FCSTD DOCUMENT  (FreeCAD 1.0RUnknown)
Label: wardrobe_corpus03_jan_assy4
License: All rights reserved
LicenseURL: https://en.wikipedia.org/wiki/All_rights_reserved
objects: App::Link×7, App::DocumentObjectGroup×3, Part::FeaturePython×2, PartDesign::CoordinateSystem×1, App::FeaturePython×1, App::Part×1, Assembly::BomObject×1
note: 3 computed .brp shape members not serialized (recipe doc carries the construction recipe); baked Part::Feature solids carry a one-line shape summary decoded from their .brp
EXTERNAL_REF file=parts/wardrobe_base_corpus03_jan.FCStd obj=LCS_Origin
EXTERNAL_REF file=parts/wardrobe_base_corpus03_jan.FCStd obj=wardrobe_base_corpus03_jan
EXTERNAL_REF file=parts/wardrobe_base_corpus03_jan.FCStd obj=LCS_1
EXTERNAL_REF file=parts/wardrobe_left_corpus03_jan.FCStd obj=LCS_1
EXTERNAL_REF file=parts/wardrobe_left_corpus03_jan.FCStd obj=wardrobe_left_corpus03_jan
EXTERNAL_REF file=parts/wardrobe_base_corpus03_jan.FCStd obj=LCS_right
EXTERNAL_REF file=parts/wardrobe_right_corpus03_jan.FCStd obj=LCS_1
EXTERNAL_REF file=parts/wardrobe_right_corpus03_jan.FCStd obj=wardrobe_right_corpus03_jan
EXTERNAL_REF file=parts/wardrobe_left_corpus03_jan.FCStd obj=LCS_2
EXTERNAL_REF file=parts/wardrobe_top_corpus03_jan.FCStd obj=LCS_1
EXTERNAL_REF file=parts/wardrobe_top_corpus03_jan.FCStd obj=wardrobe_top_corpus03_jan
EXTERNAL_REF file=../purchased parts/hettich-level-adjustment.FCStd obj=LCS_Origin
EXTERNAL_REF file=parts/wardrobe_base_corpus03_jan.FCStd obj=LCS_2
EXTERNAL_REF file=../purchased parts/hettich-level-adjustment.FCStd obj=hettich_level_adjustment
EXTERNAL_REF file=../mastersketch.FCStd obj=Sketch001
EXTERNAL_REF file=parts/wardrobe_backplate_corpus03_jan.FCStd obj=LCS_1
EXTERNAL_REF file=parts/wardrobe_base_corpus03_jan.FCStd obj=LCS_back
EXTERNAL_REF file=parts/wardrobe_backplate_corpus03_jan.FCStd obj=wardrobe_backplate_corpus03_jan
EXTERNAL_REF file=parts/wardrobe_base_corpus03_jan.FCStd obj=LCS_door
EXTERNAL_REF file=parts/wardrobe_door_03_jan.FCStd obj=LCS_Origin
EXTERNAL_REF file=parts/wardrobe_door_03_jan.FCStd obj=wardrobe_door_03_jan

FEATURE [App::DocumentObjectGroup] Parts
FEATURE [PartDesign::CoordinateSystem] LCS_Origin
  AttacherType = Attacher::AttachEngine3D
  AttachmentSupport = -> [X_Axis]
  MapMode = 2
FEATURE [App::DocumentObjectGroup] Constraints
FEATURE [App::FeaturePython] Variables  # WARN: FeaturePython — macro-defined, semantics opaque (R4)
  Type = App::PropertyContainer
FEATURE [App::DocumentObjectGroup] Configurations
FEATURE [App::Link] wardrobe_base_corpus03_jan001
  AttachedBy = #LCS_Origin
  AttachedTo = Parent Assembly#LCS_Origin
  LinkedObject = -> <external parts/wardrobe_base_corpus03_jan.FCStd>#wardrobe_base_corpus03_jan
  SolverId = Asm4EE
  expr: Placement = LCS_Origin.Placement * AttachmentOffset * wardrobe_base_corpus03_jan#LCS_Origin.Placement ^ -1
FEATURE [App::Link] wardrobe_left_corpus03_jan001
  AttachedBy = #LCS_1
  AttachedTo = wardrobe_base_corpus03_jan001#LCS_1
  AttachmentOffset = pos=(0,0,0) rot=(0,1,0;3.14159rad)
  LinkPlacement = pos=(-260,300,19) rot=(0,0,1;4.71239rad)
  LinkedObject = -> <external parts/wardrobe_left_corpus03_jan.FCStd>#wardrobe_left_corpus03_jan
  Placement = pos=(-260,300,19) rot=(0,0,1;4.71239rad)
  SolverId = Asm4EE
  expr: Placement = wardrobe_base_corpus03_jan001.Placement * wardrobe_base_corpus03_jan#LCS_1.Placement * AttachmentOffset * wardrobe_left_corpus03_jan#LCS_1.Placement ^ -1
FEATURE [App::Link] wardrobe_right_corpus03_jan001
  AttachedBy = #LCS_1
  AttachedTo = wardrobe_base_corpus03_jan001#LCS_right
  LinkPlacement = pos=(260,300,19) rot=(0,0,1;0rad)
  LinkedObject = -> <external parts/wardrobe_right_corpus03_jan.FCStd>#wardrobe_right_corpus03_jan
  Placement = pos=(260,300,19) rot=(0,0,1;0rad)
  SolverId = Asm4EE
  expr: Placement = wardrobe_base_corpus03_jan001.Placement * wardrobe_base_corpus03_jan#LCS_right.Placement * AttachmentOffset * wardrobe_right_corpus03_jan#LCS_1.Placement ^ -1
FEATURE [App::Link] wardrobe_top_corpus03_jan001
  AttachedBy = #LCS_1
  AttachedTo = wardrobe_left_corpus03_jan001#LCS_2
  AttachmentOffset = pos=(0,0,0) rot=(0,1,0;3.14159rad)
  LinkPlacement = pos=(5.68e-14,300,465.913) rot=(0,1,0;5.41956rad)
  LinkedObject = -> <external parts/wardrobe_top_corpus03_jan.FCStd>#wardrobe_top_corpus03_jan
  Placement = pos=(5.68e-14,300,465.913) rot=(0,1,0;5.41956rad)
  SolverId = Asm4EE
  expr: Placement = wardrobe_left_corpus03_jan001.Placement * wardrobe_left_corpus03_jan#LCS_2.Placement * AttachmentOffset * wardrobe_top_corpus03_jan#LCS_1.Placement ^ -1
FEATURE [App::Link] hettich_level_adjustment
  AttachedBy = #LCS_Origin
  AttachedTo = wardrobe_base_corpus03_jan001#LCS_2
  AttachmentOffset = pos=(0,0,0) rot=(0.707107,0.707107,0;3.14159rad)
  LinkPlacement = pos=(-220,-230,0) rot=(0.707107,0.707107,0;3.14159rad)
  LinkedObject = -> <external ../purchased parts/hettich-level-adjustment.FCStd>#hettich_level_adjustment
  Placement = pos=(-220,-230,0) rot=(0.707107,0.707107,0;3.14159rad)
  SolverId = Asm4EE
  expr: Placement = wardrobe_base_corpus03_jan001.Placement * wardrobe_base_corpus03_jan#LCS_2.Placement * AttachmentOffset * hettich_level_adjustment#LCS_Origin.Placement ^ -1
FEATURE [Part::FeaturePython] Linear_hettich_level_adjustment  # Draft array (typed FeaturePython)
  ArrayType = Linear Array
  Axis = -> X_Axis
  AxisPlacement = pos=(0,0,0) rot=(0.57735,0.57735,0.57735;2.0944rad)
  Count = 2
  Index = 1
  LinearStep = 440
  PlacementList = 2 placements: [(-220,-230,6.31089e-30),(220,-230,4.88498e-14)]
  Placer = pos=(0,0,440) rot=(0,0,1;0rad)
  ScaleList = (2) [(1,1,1),(1,1,1)]
  Scaler = 1
  ShowElement = false
  SourceObject = -> hettich_level_adjustment
  expr: .Placer.Base.z = LinearStep * Index
  expr: LinearStep = mastersketch#<<corpus>>.Constraints.corpus_width - 100 mm
FEATURE [Part::FeaturePython] Linear_Linear_hettich_level_adjustment  # Draft array (typed FeaturePython)
  ArrayType = Linear Array
  Axis = -> Y_Axis
  AxisPlacement = pos=(0,0,0) rot=(1,1,1;4.18879rad)
  Count = 2
  Index = 1
  LinearStep = 460
  PlacementList = 2 placements: [(0,0,0),(5.10703e-14,460,-1.53211e-13)]
  Placer = pos=(0,0,460) rot=(0,0,1;0rad)
  ScaleList = (2) [(1,1,1),(1,1,1)]
  Scaler = 1
  ShowElement = false
  SourceObject = -> Linear_hettich_level_adjustment
  expr: .Placer.Base.z = LinearStep * Index
FEATURE [App::Link] wardrobe_backplate_corpus03_jan001
  AttachedBy = #LCS_1
  AttachedTo = wardrobe_base_corpus03_jan001#LCS_back
  AttachmentOffset = pos=(0,0,0) rot=(0,0,1;1.5708rad)
  LinkPlacement = pos=(260,309,-1.4e-15) rot=(1,0,0;1.5708rad)
  LinkedObject = -> <external parts/wardrobe_backplate_corpus03_jan.FCStd>#wardrobe_backplate_corpus03_jan
  Placement = pos=(260,309,-1.4e-15) rot=(1,0,0;1.5708rad)
  SolverId = Asm4EE
  expr: Placement = wardrobe_base_corpus03_jan001.Placement * wardrobe_base_corpus03_jan#LCS_back.Placement * AttachmentOffset * wardrobe_backplate_corpus03_jan#LCS_1.Placement ^ -1
FEATURE [App::Link] wardrobe_door_03_jan
  AttachedBy = #LCS_Origin
  AttachedTo = wardrobe_base_corpus03_jan001#LCS_door
  AttachmentOffset = pos=(2.5,0,0) rot=(0,-0.707107,0.707107;3.14159rad)
  LinkPlacement = pos=(257.5,-300,0) rot=(1,0,0;1.5708rad)
  LinkedObject = -> <external parts/wardrobe_door_03_jan.FCStd>#wardrobe_door_03_jan
  Placement = pos=(257.5,-300,0) rot=(1,0,0;1.5708rad)
  SolverId = Asm4EE
  expr: Placement = wardrobe_base_corpus03_jan001.Placement * wardrobe_base_corpus03_jan#LCS_door.Placement * AttachmentOffset * wardrobe_door_03_jan#LCS_Origin.Placement ^ -1
FEATURE [App::Part] Assembly  label="wardrobe_corpus03_jan"
  AssemblyType = Part::Link
  DrawingName = wardrobe_corpus03_jan_assy4.FCStd
  Group = -> [LCS_Origin,Constraints,Variables,Configurations,wardrobe_base_corpus03_jan001,wardrobe_left_corpus03_jan001,wardrobe_right_corpus03_jan001,wardrobe_top_corpus03_jan001,hettich_level_adjustment,Linear_hettich_level_adjustment,Linear_Linear_hettich_level_adjustment,wardrobe_backplate_corpus03_jan001,wardrobe_door_03_jan]
  Origin = -> Origin
  PartID = wardrobe_corpus03_jan_assy4
  Type = Assembly
FEATURE [Assembly::BomObject] Bill_of_Materials
  cells = A1='Index; B1='Name; C1='Description; D1='File Name; E1='Quantity; A2='1; B2='wardrobe_corpus03_jan; D2='<userpath>/Projekte/attic-furniture/wardrobe_jan/subassemblies/wardrobe_corpus03_jan_assy4.FCStd; E2=1; A3='1.1; B3='wardrobe_base_corpus03_jan001; D3='<userpath>/Projekte/attic-furniture/wardrobe_jan/subassemblies/parts/wardrobe_base_corpus03_jan.FCStd; E3=1; A4='1.2; B4='wardrobe_left_corpus03_jan001; D4='<userpath>/Projekte/attic-furniture/wardrobe_jan/subassemblies/parts/wardrobe_left_corpus03_jan.FCStd; E4=1; A5='1.3; B5='wardrobe_right_corpus03_jan001; D5='<userpath>/Projekte/attic-furniture/wardrobe_jan/subassemblies/parts/wardrobe_right_corpus03_jan.FCStd; E5=1; A6='1.4; B6='wardrobe_top_corpus03_jan001; D6='<userpath>/Projekte/attic-furniture/wardrobe_jan/subassemblies/parts/wardrobe_top_corpus03_jan.FCStd; E6=1; A7='1.5; B7='hettich_level_adjustment; D7='<userpath>/Projekte/attic-furniture/wardrobe_jan/purchased parts/hettich-level-adjustment.FCStd; E7=1; A8='1.6; B8='wardrobe_backplate_corpus03_jan001; D8='<userpath>/Projekte/attic-furniture/wardrobe_jan/subassemblies/parts/wardrobe_backplate_corpus03_jan.FCStd; E8=1; A9='1.7; B9='wardrobe_door_03_jan; D9='<userpath>/Projekte/attic-furniture/wardrobe_jan/subassemblies/parts/wardrobe_door_03_jan.FCStd; E9=1
  columnsNames = Index | Name | Description | File Name | Quantity
  detailParts = true
  detailSubAssemblies = false
  onlyParts = true

RESOLVED EXTERNAL PARTS (link-assembly join: the EXTERNAL_REF files above that resolve inside this repo's crawl, each included once):
---- part ../mastersketch.FCStd = doc fcstd_204cd9ce44db ----
FCSTD DOCUMENT  (FreeCAD 1.0RUnknown)
Label: mastersketch
License: All rights reserved
LicenseURL: https://en.wikipedia.org/wiki/All_rights_reserved
objects: Sketcher::SketchObject×2, PartDesign::Body×1, Spreadsheet::Sheet×1
note: 5 computed .brp shape members not serialized (recipe doc carries the construction recipe); baked Part::Feature solids carry a one-line shape summary decoded from their .brp

FEATURE [Sketcher::SketchObject] Sketch  label="doors"
  ArcFitTolerance = 1e-06
  AttachmentSupport = -> [XZ_Plane]
  FullyConstrained = true
  MakeInternals = false
  MapMode = 5
  Placement = pos=(0,0,0) rot=(1,0,0;1.5708rad)
  expr: Constraints[23] = Spreadsheet.corpus_width - 5
  expr: Constraints[33] = Spreadsheet.hettich_height
  expr: Constraints[46] = Spreadsheet.corpus_width - 5
  expr: Constraints[58] = Spreadsheet.corpus_width - 5
  sketch-geometry (29):
    g0: LineSegment StartX=0 StartY=0 StartZ=0 EndX=0 EndY=2480 EndZ=0
    g1: LineSegment StartX=0 StartY=2480 StartZ=0 EndX=-220 EndY=2480 EndZ=0
    g2: LineSegment StartX=0 StartY=0 StartZ=0 EndX=-2160 EndY=0 EndZ=0
    g3: LineSegment StartX=-2160 StartY=0 StartZ=0 EndX=-2160 EndY=210 EndZ=0
    g4: LineSegment StartX=-2160 StartY=210 StartZ=0 EndX=-220 EndY=2480 EndZ=0
    g5: LineSegment StartX=-12.5 StartY=30 StartZ=0 EndX=-12.5 EndY=2081.4 EndZ=0
    g6: LineSegment StartX=-12.5 StartY=2081.4 StartZ=0 EndX=-547.5 EndY=2081.4 EndZ=0
    g7: LineSegment StartX=-547.5 StartY=2081.4 StartZ=0 EndX=-547.5 EndY=30 EndZ=0
    g8: LineSegment StartX=-547.5 StartY=30 StartZ=0 EndX=-12.5 EndY=30 EndZ=0
    g9: LineSegment StartX=-2160 StartY=194.608 StartZ=0 EndX=-206.846 EndY=2480 EndZ=0
    g10: LineSegment StartX=-2160 StartY=30 StartZ=0 EndX=0 EndY=30 EndZ=0
    g11: LineSegment StartX=-552.5 StartY=30 StartZ=0 EndX=-552.5 EndY=1449.54 EndZ=0
    g12: LineSegment StartX=-552.5 StartY=1449.54 StartZ=0 EndX=-1087.5 EndY=1449.54 EndZ=0
    g13: LineSegment StartX=-1087.5 StartY=1449.54 StartZ=0 EndX=-1087.5 EndY=30 EndZ=0
    g14: LineSegment StartX=-1087.5 StartY=30 StartZ=0 EndX=-552.5 EndY=30 EndZ=0
    g15: LineSegment StartX=-1627.5 StartY=30 StartZ=0 EndX=-1092.5 EndY=30 EndZ=0
    g16: LineSegment StartX=-1092.5 StartY=30 StartZ=0 EndX=-1092.5 EndY=817.688 EndZ=0
    g17: LineSegment StartX=-1092.5 StartY=817.688 StartZ=0 EndX=-1627.5 EndY=817.688 EndZ=0
    g18: LineSegment StartX=-1627.5 StartY=817.688 StartZ=0 EndX=-1627.5 EndY=30 EndZ=0
    g19: LineSegment StartX=-1632.5 StartY=811.837 StartZ=0 EndX=-1632.5 EndY=30 EndZ=0
    g20: LineSegment StartX=-12.5 StartY=2081.4 StartZ=0 EndX=-12.5 EndY=2470 EndZ=0
    g21: LineSegment StartX=-552.5 StartY=1449.54 StartZ=0 EndX=-552.5 EndY=2075.55 EndZ=0
    g22: LineSegment StartX=-1092.5 StartY=817.688 StartZ=0 EndX=-1092.5 EndY=1443.69 EndZ=0
    g23: LineSegment [constr] StartX=-12.5 StartY=2470 StartZ=0 EndX=-215.392 EndY=2470 EndZ=0
    g24: LineSegment [constr] StartX=-2147.5 StartY=209.234 StartZ=0 EndX=-2147.5 EndY=30 EndZ=0
    g25: LineSegment [constr] StartX=-2150 StartY=177.064 StartZ=0 EndX=-1627.5 EndY=788.443 EndZ=0
    g26: LineSegment [constr] StartX=-1904.57 StartY=493.489 StartZ=0 EndX=-1890.12 EndY=481.145 EndZ=0
    g27: LineSegment [constr] StartX=-2147.5 StartY=49 StartZ=0 EndX=-1627.5 EndY=49 EndZ=0
    g28: LineSegment [constr] StartX=-2150 StartY=177.064 StartZ=0 EndX=-2150 EndY=49 EndZ=0
  constraints (107):
    c: Distance(g0) = 2480
    c: Coincident(g0,g-1)
    c: PointOnObject(g0,g-2)
    c: Distance(g1) = 220
    c: Coincident(g1,g0)
    c: Horizontal(g1)
    c: Distance(g2) = 2160
    c: Coincident(g2,g0)
    c: PointOnObject(g2,g-1)
    c: Distance(g3) = 210
    c: Coincident(g3,g2)
    c: Vertical(g3)
    c: Coincident(g4,g3)
    c: Coincident(g4,g1)
    c: Coincident(g5,g6)
    c: Coincident(g6,g7)
    c: Coincident(g7,g8)
    c: Coincident(g8,g5)
    c: Vertical(g5)
    c: Vertical(g7)
    c: Horizontal(g6)
    c: Horizontal(g8)
    c: Distance(g0,g5) = 12.5
    c: DistanceX(g6,g6) = 535
    c: DistanceY(g5,g5) = 2051.4  'corpus00_height'
    c: PointOnObject(g9,g3)
    c: PointOnObject(g9,g1)
    c: Parallel(g4,g9)
    c: Distance(g3,g9) = 10
    c: PointOnObject(g6,g9)
    c: PointOnObject(g10,g3)
    c: PointOnObject(g10,g0)
    c: Horizontal(g10)
    c: Distance(g2,g10) = 30
    c: PointOnObject(g7,g10)
    c: Coincident(g11,g12)
    c: Coincident(g12,g13)
    c: Coincident(g13,g14)
    c: Coincident(g14,g11)
    c: Vertical(g11)
    c: Vertical(g13)
    c: Horizontal(g12)
    c: Horizontal(g14)
    c: PointOnObject(g11,g10)
    c: PointOnObject(g12,g9)
    c: Distance(g7,g11) = 5
    c: DistanceX(g12,g12) = 535
    c: Distance(g10,g12) = 1419.54  'corpus01_height'
    c: Coincident(g15,g16)
    c: Coincident(g16,g17)
    c: Coincident(g17,g18)
    c: Coincident(g18,g15)
    c: Horizontal(g15)
    c: Horizontal(g17)
    c: Vertical(g16)
    c: Vertical(g18)
    c: PointOnObject(g15,g10)
    c: PointOnObject(g17,g9)
    c: Distance(g16,g18) = 535
    c: Distance(g10,g17) = 787.688  'corpus02_height'
    c: Distance(g13,g16) = 5
    c: PointOnObject(g19,g9)
    c: PointOnObject(g19,g10)
    c: Vertical(g19)
    c: Distance(g18,g19) = 5
    c: DistanceY(g19,g19) = 781.837  'corpus03_door_height'
    c: Coincident(g20,g5)
    c: Vertical(g20)
    c: Distance(g20,g1) = 10
    c: Distance(g20,g8) = 2440  'corpus00_door_height'
    c: Coincident(g21,g11)
    c: Vertical(g21)
    c: Distance(g21,g10) = 2045.55  'corpus01_door_height'
    c: Coincident(g22,g16)
    c: Vertical(g22)
    c: PointOnObject(g21,g9)
    c: PointOnObject(g22,g9)
    c: Distance(g22,g10) = 1413.69  'corpus02_door_height'
    c: Angle(g3,g4) = 2.43442  'alpha'
    c: Distance(g6,g8) = 2051.4
    c: Coincident(g23,g20)
    c: PointOnObject(g23,g9)
    c: Horizontal(g23)
    c: DistanceX(g23,g23) = 202.892  'corpus00_door_top'
    c: PointOnObject(g24,g10)
    c: Vertical(g24)
    c: Distance(g3,g24) = 12.5
    c: Distance(g19,g24) = 515  'corpus03_door_width'
    c: PointOnObject(g25,g18)
    c: Parallel(g25,g9)
    c: PointOnObject(g26,g9)
    c: PointOnObject(g26,g25)
    c: Perpendicular(g25,g26)
    c: Distance(g26,g25) = 400
    c: Distance(g26,g26) = 19
    c: Distance(g25,g25) = 804.233  'corpus03_top'
    c: PointOnObject(g27,g24)
    c: PointOnObject(g27,g18)
    c: Horizontal(g27)
    c: Distance(g10,g27) = 19
    c: DistanceY(g27,g25) = 739.443  'corpus03_right_height'
    c: Vertical(g28)
    c: Horizontal(g28,g27)
    c: Distance(g28,g3) = 10
    c: DistanceY(g28,g28) = 128.064  'corpus03_left_height'
    c: Coincident(g28,g25)
    c: PointOnObject(g24,g9)
FEATURE [Sketcher::SketchObject] Sketch001  label="corpus"
  ArcFitTolerance = 1e-06
  AttachmentOffset = pos=(0,0,-20) rot=(0,0,1;0rad)
  AttachmentSupport = -> [XZ_Plane]
  ExternalGeometry = -> [Sketch]
  FullyConstrained = true
  MakeInternals = false
  MapMode = 5
  Placement = pos=(0,20,-4.4e-15) rot=(1,0,0;1.5708rad)
  expr: Constraints[22] = .Constraints.corpus_width
  expr: Constraints[33] = .Constraints.corpus_width
  expr: Constraints[55] = <<doors>>.Constraints.alpha
  expr: Constraints[65] = <<doors>>.Constraints.alpha
  sketch-geometry (29):
    g0: LineSegment StartX=-550 StartY=2078.47 StartZ=0 EndX=-550 EndY=30 EndZ=0
    g1: LineSegment StartX=-550 StartY=30 StartZ=0 EndX=-10 EndY=30 EndZ=0
    g2: LineSegment StartX=-10 StartY=30 StartZ=0 EndX=-10 EndY=2078.47 EndZ=0
    g3: LineSegment StartX=-10 StartY=2078.47 StartZ=0 EndX=-550 EndY=2078.47 EndZ=0
    g4: LineSegment StartX=-550 StartY=30 StartZ=0 EndX=-550 EndY=1446.62 EndZ=0
    g5: LineSegment StartX=-550 StartY=1446.62 StartZ=0 EndX=-1090 EndY=1446.62 EndZ=0
    g6: LineSegment StartX=-1090 StartY=1446.62 StartZ=0 EndX=-1090 EndY=30 EndZ=0
    g7: LineSegment StartX=-1090 StartY=30 StartZ=0 EndX=-550 EndY=30 EndZ=0
    g8: LineSegment StartX=-1090 StartY=30 StartZ=0 EndX=-1090 EndY=814.763 EndZ=0
    g9: LineSegment StartX=-1090 StartY=814.763 StartZ=0 EndX=-1630 EndY=814.763 EndZ=0
    g10: LineSegment StartX=-1630 StartY=814.763 StartZ=0 EndX=-1630 EndY=30 EndZ=0
    g11: LineSegment StartX=-1630 StartY=30 StartZ=0 EndX=-1090 EndY=30 EndZ=0
    g12: LineSegment StartX=-2150 StartY=30 StartZ=0 EndX=-1630 EndY=30 EndZ=0
    g13: LineSegment StartX=-1630 StartY=30 StartZ=0 EndX=-1630 EndY=49 EndZ=0
    g14: LineSegment StartX=-1630 StartY=49 StartZ=0 EndX=-2150 EndY=49 EndZ=0
    g15: LineSegment StartX=-2150 StartY=49 StartZ=0 EndX=-2150 EndY=30 EndZ=0
    g16: LineSegment StartX=-1649 StartY=49 StartZ=0 EndX=-1630 EndY=49 EndZ=0
    g17: LineSegment StartX=-1630 StartY=49 StartZ=0 EndX=-1630 EndY=785.518 EndZ=0
    g18: LineSegment StartX=-1649 StartY=763.286 StartZ=0 EndX=-1649 EndY=49 EndZ=0
    g19: LineSegment StartX=-1630 StartY=785.518 StartZ=0 EndX=-1649 EndY=763.286 EndZ=0
    g20: LineSegment StartX=-2150 StartY=49 StartZ=0 EndX=-2131 EndY=49 EndZ=0
    g21: LineSegment StartX=-2131 StartY=49 StartZ=0 EndX=-2131 EndY=199.296 EndZ=0
    g22: LineSegment StartX=-2150 StartY=177.064 StartZ=0 EndX=-2150 EndY=49 EndZ=0
    g23: LineSegment StartX=-2131 StartY=199.296 StartZ=0 EndX=-2150 EndY=177.064 EndZ=0
    g24: LineSegment StartX=-2150 StartY=177.064 StartZ=0 EndX=-2150 EndY=206.309 EndZ=0
    g25: LineSegment StartX=-2150 StartY=206.309 StartZ=0 EndX=-1630 EndY=814.763 EndZ=0
    g26: LineSegment StartX=-1630 StartY=814.763 StartZ=0 EndX=-1630 EndY=785.518 EndZ=0
    g27: LineSegment StartX=-1630 StartY=785.518 StartZ=0 EndX=-2150 EndY=177.064 EndZ=0
    g28: LineSegment [constr] StartX=-2150 StartY=206.309 StartZ=0 EndX=-2135.56 EndY=193.965 EndZ=0
  constraints (86):
    c: Coincident(g0,g1)
    c: Coincident(g1,g2)
    c: Coincident(g2,g3)
    c: Coincident(g3,g0)
    c: Vertical(g0)
    c: Vertical(g2)
    c: Horizontal(g1)
    c: Horizontal(g3)
    c: PointOnObject(g1,g-8)
    c: Distance(g-5,g2) = 10
    c: Distance(g2,g0) = 540  'corpus_width'
    c: Coincident(g4,g5)
    c: Coincident(g5,g6)
    c: Coincident(g6,g7)
    c: Coincident(g7,g4)
    c: Vertical(g4)
    c: Vertical(g6)
    c: Horizontal(g5)
    c: Horizontal(g7)
    c: Coincident(g4,g0)
    c: PointOnObject(g0,g-9)
    c: PointOnObject(g5,g-9)
    c: DistanceX(g6,g0) = 540
    c: Coincident(g8,g9)
    c: Coincident(g9,g10)
    c: Coincident(g10,g11)
    c: Coincident(g11,g8)
    c: Vertical(g8)
    c: Vertical(g10)
    c: Horizontal(g9)
    c: Horizontal(g11)
    c: Coincident(g8,g6)
    c: PointOnObject(g9,g-9)
    c: DistanceX(g10,g6) = 540
    c: Coincident(g12,g13)
    c: Coincident(g13,g14)
    c: Coincident(g14,g15)
    c: Coincident(g15,g12)
    c: Horizontal(g12)
    c: Horizontal(g14)
    c: Vertical(g13)
    c: Vertical(g15)
    c: PointOnObject(g12,g-8)
    c: PointOnObject(g13,g10)
    c: Distance(g12,g14) = 19
    c: DistanceX(g-8,g12) = 10
    c: Coincident(g16,g17)
    c: Coincident(g18,g16)
    c: Horizontal(g16)
    c: Vertical(g17)
    c: Vertical(g18)
    c: PointOnObject(g16,g14)
    c: PointOnObject(g17,g10)
    c: Coincident(g19,g17)
    c: Coincident(g18,g19)
    c: Angle(g18,g19) = 2.43442
    c: Distance(g16,g13) = 19
    c: Coincident(g20,g21)
    c: Coincident(g22,g20)
    c: Horizontal(g20)
    c: Vertical(g21)
    c: Vertical(g22)
    c: Coincident(g20,g14)
    c: Coincident(g23,g21)
    c: Coincident(g22,g23)
    c: Angle(g22,g23) = 2.43442
    c: Distance(g14,g20) = 19
    c: Coincident(g24,g22)
    c: Vertical(g24)
    c: Coincident(g25,g24)
    c: PointOnObject(g25,g10)
    c: Coincident(g26,g25)
    c: Coincident(g26,g17)
    c: Coincident(g27,g17)
    c: Coincident(g27,g22)
    c: Parallel(g27,g25)
    c: Parallel(g25,g-9)
    c: Coincident(g28,g24)
    c: PointOnObject(g28,g23)
    c: Perpendicular(g27,g28)
    c: Distance(g28,g28) = 19
    c: PointOnObject(g25,g-9)
    c: DistanceY(g13,g17) = 736.518  'corpus03_right_height'
    c: DistanceY(g22,g22) = 128.064  'corpus03_left_height'
    c: DistanceY(g10,g9) = 784.763  'corpus03_back_height'
    c: DistanceX(g14,g10) = 520  'corpus03_width'
FEATURE [PartDesign::Body] Body
  AllowCompound = false
  Group = -> [Sketch,Sketch001]
  Origin = -> Origin
FEATURE [Spreadsheet::Sheet] Spreadsheet
  cells = A1='corpus_width; B1(corpus_width)=540; A2='corpus_depth; B2(corpus_depth)=600; A3='corpus_outer_thickness; B3(corpus_outer_thickness)=19; A4='corpus_backplate_thickness; B4(corpus_backplate_thickness)=19; A5='corpus_heigth; B5(corpus_height)=2045; A6='corpus01_heigth; B6(corpus01_height)=1415; A7='corpus02_heigth; B7(corpus02_height)=780; A8='drawer_outer_thickness; B8(drawer_outer_thickness)=19; A9='drawer_bottom_thickness; B9(drawer_bottom_thickness)=6; A10='drawer_length; B10(drawer_length)==B2 - 50; A11='drawer_width; B11(drawer_width)==B1 - 2 * 12.5 - 2 * B3; A12='drawer_bottom_tol; B12(drawer_bottom_tol)=0.5; A13='drawer_height; B13(drawer_height)=170; A14='drawer_slot_depth; B14(drawer_slot_depth)=8; A15='drawer_slot_height; B15(drawer_slot_height)=10; A16='hettich_height; B16(hettich_height)=30
---- part parts/wardrobe_backplate_corpus03_jan.FCStd = doc fcstd_d5a495dcd873 ----
FCSTD DOCUMENT  (FreeCAD 1.0RUnknown)
Label: wardrobe_backplate_corpus03_jan
License: All rights reserved
LicenseURL: https://en.wikipedia.org/wiki/All_rights_reserved
objects: TechDraw::DrawViewDimension×6, PartDesign::CoordinateSystem×2, TechDraw::DrawProjGroupItem×2, Sketcher::SketchObject×1, PartDesign::Pad×1, PartDesign::Body×1, App::Part×1, TechDraw::DrawSVGTemplate×1, TechDraw::DrawPage×1
note: 16 computed .brp shape members not serialized (recipe doc carries the construction recipe); baked Part::Feature solids carry a one-line shape summary decoded from their .brp
EXTERNAL_REF file=../../mastersketch.FCStd obj=Sketch
EXTERNAL_REF file=../../mastersketch.FCStd obj=Sketch001

FEATURE [Sketcher::SketchObject] Sketch
  ArcFitTolerance = 1e-06
  AttachmentSupport = -> [XY_Plane]
  FullyConstrained = true
  MakeInternals = false
  MapMode = 5
  expr: Constraints[0] = mastersketch#<<corpus>>.Constraints.corpus03_back_height
  expr: Constraints[10] = mastersketch#Sketch.Constraints.alpha
  expr: Constraints[3] = mastersketch#Sketch.Constraints.corpus03_door_width + 5 mm
  sketch-geometry (4):
    g0: LineSegment StartX=0 StartY=0 StartZ=0 EndX=0 EndY=784.763 EndZ=0
    g1: LineSegment StartX=0 StartY=0 StartZ=0 EndX=-520 EndY=0 EndZ=0
    g2: LineSegment StartX=-520 StartY=0 StartZ=0 EndX=-520 EndY=176.309 EndZ=0
    g3: LineSegment StartX=-520 StartY=176.309 StartZ=0 EndX=0 EndY=784.763 EndZ=0
  constraints (11):
    c: Distance(g0) = 784.763
    c: Coincident(g0,g-1)
    c: Vertical(g0)
    c: Distance(g1) = 520
    c: Coincident(g1,g0)
    c: PointOnObject(g1,g-1)
    c: Vertical(g2)
    c: Coincident(g3,g2)
    c: Coincident(g2,g1)
    c: Coincident(g3,g0)
    c: Angle(g2,g3) = 2.43442
FEATURE [PartDesign::Pad] Pad
  Direction = (0,0,1)
  Length = 9
  Length2 = 10
  Profile = -> Sketch
  ReferenceAxis = -> Sketch [N_Axis]
  Refine = true
  Suppressed = false
  Type = 0
FEATURE [PartDesign::Body] Body  label="wardrobe_backplate_corpus03_jan"
  AllowCompound = false
  Group = -> [Sketch,Pad]
  Origin = -> Origin
  Tip = -> Pad
FEATURE [PartDesign::CoordinateSystem] LCS_1
  AttacherType = Attacher::AttachEngine3D
  AttachmentSupport = -> [Pad]
  MapMode = 45
  Placement = pos=(-260,0,9) rot=(0.57735,0.57735,0.57735;2.0944rad)
FEATURE [PartDesign::CoordinateSystem] LCS_Origin
  AttacherType = Attacher::AttachEngine3D
  AttachmentSupport = -> [X_Axis001]
  MapMode = 2
FEATURE [App::Part] wardrobe_backplate_corpus03_jan  label="wardrobe_backplate_corpus03_jan001"
  DrawingName = wardrobe_backplate_corpus03_jan.FCStd
  Group = -> [LCS_Origin,Body,LCS_1]
  Origin = -> Origin001
  PartDescription = wardrobe_backplate_corpus03_jan
  PartID = wardrobe_backplate_corpus03_jan
FEATURE [TechDraw::DrawSVGTemplate] Template  label="Vorlage"
  Height = 210
  Orientation = 1
  Template = <userpath>/scoop/apps/freecad/current/data/Mod/TechDraw/Templates/A4_Landscape_TD.svg
  Width = 297
FEATURE [TechDraw::DrawProjGroupItem] View
  CoarseView = false
  Direction = (0,0,-1)
  Focus = 100
  HardHidden = false
  IsoCount = 0
  IsoHidden = false
  IsoVisible = false
  LockPosition = false
  Perspective = false
  Rotation = 0
  RotationVector = (1,0,0)
  Scale = 0.1
  ScaleType = 2
  ScrubCount = 1
  SeamHidden = false
  SeamVisible = false
  SmoothHidden = false
  SmoothVisible = true
  Source = -> [wardrobe_backplate_corpus03_jan]
  Type = 0
  X = 139.342
  XDirection = (1e-16,-1,0)
  Y = 152.765
FEATURE [TechDraw::DrawProjGroupItem] View001
  CoarseView = false
  Direction = (-1,1e-16,0)
  Focus = 100
  HardHidden = false
  IsoCount = 0
  IsoHidden = false
  IsoVisible = false
  LockPosition = false
  Perspective = false
  Rotation = 0
  RotationVector = (1,0,0)
  Scale = 0.1
  ScaleType = 2
  ScrubCount = 1
  SeamHidden = false
  SeamVisible = false
  SmoothHidden = false
  SmoothVisible = true
  Source = -> [wardrobe_backplate_corpus03_jan]
  Type = 0
  X = 139.342
  XDirection = (-1e-16,-1,-1e-16)
  Y = 95.3896
FEATURE [TechDraw::DrawViewDimension] Dimension  label="Maß"
  AngleOverride = false
  Arbitrary = false
  ArbitraryTolerances = false
  BoxCorners = (2) [(-39.2381,-26,0),(39.2381,26,0)]
  EqualTolerance = true
  ExtensionAngle = 0
  FormatSpec = %.1w
  FormatSpecOverTolerance = %+.1w
  FormatSpecUnderTolerance = %+.1w
  Inverted = false
  LineAngle = 0
  LockPosition = false
  MeasureType = 1
  OverTolerance = 0
  References2D = -> [View]
  Rotation = 0
  ScaleType = 0
  TheoreticalExact = false
  Type = 2
  UnderTolerance = 0
  X = 49.6993
  Y = 0
FEATURE [TechDraw::DrawViewDimension] Dimension001  label="Maß001"
  AngleOverride = false
  Arbitrary = false
  ArbitraryTolerances = false
  BoxCorners = (2) [(-39.2381,-26,0),(39.2381,26,0)]
  EqualTolerance = true
  ExtensionAngle = 0
  FormatSpec = %.1w
  FormatSpecOverTolerance = %+.1w
  FormatSpecUnderTolerance = %+.1w
  Inverted = false
  LineAngle = 0
  LockPosition = false
  MeasureType = 1
  OverTolerance = 0
  References2D = -> [View]
  Rotation = 0
  ScaleType = 0
  TheoreticalExact = false
  Type = 1
  UnderTolerance = 0
  X = 30.4227
  Y = 41.8359
FEATURE [TechDraw::DrawViewDimension] Dimension002  label="Maß002"
  AngleOverride = false
  Arbitrary = false
  ArbitraryTolerances = false
  BoxCorners = (2) [(-39.2381,-26,0),(39.2381,26,0)]
  EqualTolerance = true
  ExtensionAngle = 0
  FormatSpec = %.1w
  FormatSpecOverTolerance = %+.1w
  FormatSpecUnderTolerance = %+.1w
  Inverted = false
  LineAngle = 0
  LockPosition = false
  MeasureType = 1
  OverTolerance = 0
  References2D = -> [View]
  Rotation = 0
  ScaleType = 0
  TheoreticalExact = false
  Type = 1
  UnderTolerance = 0
  X = 4.13456
  Y = -31.8715
FEATURE [TechDraw::DrawViewDimension] Dimension003  label="Maß003"
  AngleOverride = false
  Arbitrary = false
  ArbitraryTolerances = false
  BoxCorners = (2) [(-39.2381,-26,0),(39.2381,26,0)]
  EqualTolerance = true
  ExtensionAngle = 0
  FormatSpec = (%.1w)
  FormatSpecOverTolerance = %+.1w
  FormatSpecUnderTolerance = %+.1w
  Inverted = false
  LineAngle = 0
  LockPosition = false
  MeasureType = 1
  OverTolerance = 0
  References2D = -> [View]
  Rotation = 0
  ScaleType = 0
  TheoreticalExact = false
  Type = 6
  UnderTolerance = 0
  X = 23.687
  Y = 19.1567
FEATURE [TechDraw::DrawViewDimension] Dimension004  label="Maß004"
  AngleOverride = false
  Arbitrary = false
  ArbitraryTolerances = false
  BoxCorners = (2) [(-39.2381,-0.3,0),(39.2381,0.3,0)]
  EqualTolerance = true
  ExtensionAngle = 0
  FormatSpec = %.1w
  FormatSpecOverTolerance = %+.1w
  FormatSpecUnderTolerance = %+.1w
  Inverted = false
  LineAngle = 0
  LockPosition = false
  MeasureType = 1
  OverTolerance = 0
  References2D = -> [View001]
  Rotation = 0
  ScaleType = 0
  TheoreticalExact = false
  Type = 0
  UnderTolerance = 0
  X = 44.2586
  Y = -7.5641
FEATURE [TechDraw::DrawViewDimension] Dimension005  label="Maß005"
  AngleOverride = false
  Arbitrary = false
  ArbitraryTolerances = false
  BoxCorners = (2) [(-39.2381,-26,0),(39.2381,26,0)]
  EqualTolerance = true
  ExtensionAngle = 0
  FormatSpec = (%.2w)
  FormatSpecOverTolerance = %+.2w
  FormatSpecUnderTolerance = %+.2w
  Inverted = false
  LineAngle = 0
  LockPosition = false
  MeasureType = 1
  OverTolerance = 0
  References2D = -> [View]
  Rotation = 0
  ScaleType = 0
  TheoreticalExact = false
  Type = 0
  UnderTolerance = 0
  X = -22.0448
  Y = 15.4797
FEATURE [TechDraw::DrawPage] Page  label="Seite"
  KeepUpdated = true
  NextBalloonIndex = 1
  ProjectionType = 0
  Template = -> Template
  Views = -> [View,View001,Dimension,Dimension001,Dimension002,Dimension003,Dimension004,Dimension005]
---- part parts/wardrobe_base_corpus03_jan.FCStd = doc fcstd_a7f33c75d76e ----
FCSTD DOCUMENT  (FreeCAD 1.0RUnknown)
Label: wardrobe_base_corpus03_jan
License: All rights reserved
LicenseURL: https://en.wikipedia.org/wiki/All_rights_reserved
objects: PartDesign::CoordinateSystem×9, Sketcher::SketchObject×2, PartDesign::Pad×1, PartDesign::Body×1, App::Part×1
note: 17 computed .brp shape members not serialized (recipe doc carries the construction recipe); baked Part::Feature solids carry a one-line shape summary decoded from their .brp
EXTERNAL_REF file=../../mastersketch.FCStd obj=Sketch001
EXTERNAL_REF file=../../mastersketch.FCStd obj=Spreadsheet

FEATURE [Sketcher::SketchObject] Sketch
  ArcFitTolerance = 1e-06
  AttachmentSupport = -> [XY_Plane]
  FullyConstrained = true
  MakeInternals = false
  MapMode = 5
  expr: Constraints[10] = mastersketch#<<corpus>>.Constraints.corpus03_width
  expr: Constraints[11] = mastersketch#Spreadsheet.corpus_depth
  sketch-geometry (5):
    g0: LineSegment StartX=-260 StartY=-300 StartZ=0 EndX=260 EndY=-300 EndZ=0
    g1: LineSegment StartX=260 StartY=-300 StartZ=0 EndX=260 EndY=300 EndZ=0
    g2: LineSegment StartX=260 StartY=300 StartZ=0 EndX=-260 EndY=300 EndZ=0
    g3: LineSegment StartX=-260 StartY=300 StartZ=0 EndX=-260 EndY=-300 EndZ=0
    g4: GeomPoint [constr] X=0 Y=0 Z=0
  constraints (12):
    c: Coincident(g0,g1)
    c: Coincident(g1,g2)
    c: Coincident(g2,g3)
    c: Coincident(g3,g0)
    c: Horizontal(g0)
    c: Horizontal(g2)
    c: Vertical(g1)
    c: Vertical(g3)
    c: Symmetric(g2,g0,g4)
    c: Coincident(g4,g-1)
    c: DistanceX(g0,g0) = 520
    c: DistanceY(g3,g3) = 600
FEATURE [PartDesign::Pad] Pad
  Direction = (0,0,1)
  Length = 19
  Length2 = 10
  Profile = -> Sketch
  ReferenceAxis = -> Sketch [N_Axis]
  Refine = true
  Suppressed = false
  Type = 0
  expr: Length = mastersketch#Spreadsheet.corpus_outer_thickness
FEATURE [PartDesign::CoordinateSystem] LCS_1  label="LCS_left"
  AttacherType = Attacher::AttachEngine3D
  AttachmentSupport = -> [Pad]
  MapMode = 45
  Placement = pos=(-260,1.42e-14,19) rot=(0,0.707107,0.707107;3.14159rad)
FEATURE [PartDesign::CoordinateSystem] LCS_right  label="LCS-right"
  AttacherType = Attacher::AttachEngine3D
  AttachmentSupport = -> [Pad]
  MapMode = 45
  Placement = pos=(260,-1.42e-14,19) rot=(0,0.707107,0.707107;3.14159rad)
FEATURE [Sketcher::SketchObject] Sketch_1  label="feet_placement"
  ArcFitTolerance = 1e-06
  AttachmentSupport = -> [Pad]
  FullyConstrained = true
  MakeInternals = false
  MapMode = 5
  Placement = pos=(0,0,0) rot=(1,0,0;3.14159rad)
  expr: Constraints[10] = mastersketch#Spreadsheet.corpus_width - 100
  expr: Constraints[11] = mastersketch#Spreadsheet.corpus_depth - 140
  sketch-geometry (5):
    g0: LineSegment StartX=-220 StartY=-230 StartZ=0 EndX=220 EndY=-230 EndZ=0
    g1: LineSegment StartX=220 StartY=-230 StartZ=0 EndX=220 EndY=230 EndZ=0
    g2: LineSegment StartX=220 StartY=230 StartZ=0 EndX=-220 EndY=230 EndZ=0
    g3: LineSegment StartX=-220 StartY=230 StartZ=0 EndX=-220 EndY=-230 EndZ=0
    g4: GeomPoint [constr] X=0 Y=0 Z=0
  constraints (12):
    c: Coincident(g0,g1)
    c: Coincident(g1,g2)
    c: Coincident(g2,g3)
    c: Coincident(g3,g0)
    c: Horizontal(g0)
    c: Horizontal(g2)
    c: Vertical(g1)
    c: Vertical(g3)
    c: Symmetric(g2,g0,g4)
    c: Coincident(g4,g-1)
    c: DistanceX(g0,g0) = 440
    c: DistanceY(g3,g3) = 460
FEATURE [PartDesign::Body] Body  label="wardrobe_base_corpus03_jan"
  AllowCompound = false
  Group = -> [Sketch,Pad,Sketch_1]
  Origin = -> Origin
  Tip = -> Pad
FEATURE [PartDesign::CoordinateSystem] LCS_2  label="LCS_feet0"
  AttacherType = Attacher::AttachEngine3D
  AttachmentSupport = -> [Sketch_1]
  MapMode = 1
  Placement = pos=(-220,-230,0) rot=(0,0,1;0rad)
FEATURE [PartDesign::CoordinateSystem] LCS_feet1
  AttacherType = Attacher::AttachEngine3D
  AttachmentSupport = -> [Sketch_1]
  MapMode = 1
  Placement = pos=(220,-230,0) rot=(0,0,1;0rad)
FEATURE [PartDesign::CoordinateSystem] LCS_feet2
  AttacherType = Attacher::AttachEngine3D
  AttachmentSupport = -> [Sketch_1]
  MapMode = 1
  Placement = pos=(220,230,0) rot=(0,0,1;0rad)
FEATURE [PartDesign::CoordinateSystem] LCS_feet3
  AttacherType = Attacher::AttachEngine3D
  AttachmentSupport = -> [Sketch_1]
  MapMode = 1
  Placement = pos=(-220,230,0) rot=(0,0,1;0rad)
FEATURE [PartDesign::CoordinateSystem] LCS_back
  AttacherType = Attacher::AttachEngine3D
  AttachmentSupport = -> [Pad]
  MapMode = 45
  Placement = pos=(0,300,0) rot=(0.57735,0.57735,0.57735;2.0944rad)
FEATURE [PartDesign::CoordinateSystem] LCS_door
  AttacherType = Attacher::AttachEngine3D
  AttachmentSupport = -> [Pad]
  MapMode = 7
  Placement = pos=(260,-300,0) rot=(0,1,0;3.14159rad)
FEATURE [PartDesign::CoordinateSystem] LCS_Origin
  AttacherType = Attacher::AttachEngine3D
  AttachmentSupport = -> [X_Axis001]
  MapMode = 2
FEATURE [App::Part] wardrobe_base_corpus03_jan  label="wardrobe_base_corpus03_jan001"
  DrawingName = wardrobe_base_corpus03_jan.FCStd
  Group = -> [LCS_Origin,LCS_1,LCS_right,LCS_2,LCS_feet1,LCS_feet2,LCS_feet3,LCS_back,LCS_door,Body]
  Origin = -> Origin001
  PartDescription = wardrobe_base_corpus03_jan
  PartID = wardrobe_base_corpus03_jan
---- part parts/wardrobe_door_03_jan.FCStd = doc fcstd_eb08696c93a5 ----
FCSTD DOCUMENT  (FreeCAD 1.0R39285 (Git))
Label: wardrobe_door_03_jan
License: All rights reserved
LicenseURL: https://en.wikipedia.org/wiki/All_rights_reserved
objects: TechDraw::DrawViewDimension×6, PartDesign::CoordinateSystem×2, TechDraw::DrawProjGroupItem×2, Sketcher::SketchObject×1, PartDesign::Pad×1, PartDesign::Body×1, App::Part×1, TechDraw::DrawSVGTemplate×1, TechDraw::DrawViewAnnotation×1, TechDraw::DrawPage×1
note: 15 computed .brp shape members not serialized (recipe doc carries the construction recipe); baked Part::Feature solids carry a one-line shape summary decoded from their .brp
EXTERNAL_REF file=../../mastersketch.FCStd obj=Sketch

FEATURE [Sketcher::SketchObject] Sketch
  ArcFitTolerance = 1e-06
  AttachmentSupport = -> [XY_Plane]
  FullyConstrained = true
  MakeInternals = false
  MapMode = 5
  expr: Constraints[0] = mastersketch#Sketch.Constraints.corpus03_door_height
  expr: Constraints[10] = mastersketch#Sketch.Constraints.alpha
  expr: Constraints[3] = mastersketch#Sketch.Constraints.corpus03_door_width
  sketch-geometry (4):
    g0: LineSegment StartX=0 StartY=0 StartZ=0 EndX=0 EndY=781.837 EndZ=0
    g1: LineSegment StartX=0 StartY=0 StartZ=0 EndX=-515 EndY=0 EndZ=0
    g2: LineSegment StartX=-515 StartY=0 StartZ=0 EndX=-515 EndY=179.234 EndZ=0
    g3: LineSegment StartX=-515 StartY=179.234 StartZ=0 EndX=0 EndY=781.837 EndZ=0
  constraints (11):
    c: Distance(g0) = 781.837
    c: Coincident(g0,g-1)
    c: Vertical(g0)
    c: Distance(g1) = 515
    c: Coincident(g1,g0)
    c: PointOnObject(g1,g-1)
    c: Vertical(g2)
    c: Coincident(g3,g2)
    c: Coincident(g2,g1)
    c: Coincident(g3,g0)
    c: Angle(g2,g3) = 2.43442
FEATURE [PartDesign::Pad] Pad
  Direction = (0,0,1)
  Length = 19
  Length2 = 10
  Profile = -> Sketch
  ReferenceAxis = -> Sketch [N_Axis]
  Refine = true
  Suppressed = false
  Type = 0
FEATURE [PartDesign::Body] Body  label="wardrobe_door_corpus02_jan"
  AllowCompound = false
  Group = -> [Sketch,Pad]
  Origin = -> Origin
  Tip = -> Pad
FEATURE [PartDesign::CoordinateSystem] LCS_2
  AttacherType = Attacher::AttachEngine3D
  AttachmentSupport = -> [Pad]
  MapMode = 7
  Placement = pos=(-515,179.234,0) rot=(0.886496,-0.327204,-0.327204;1.69098rad)
FEATURE [PartDesign::CoordinateSystem] LCS_Origin
  AttacherType = Attacher::AttachEngine3D
  AttachmentSupport = -> [X_Axis001]
  MapMode = 2
FEATURE [App::Part] wardrobe_door_03_jan
  DrawingName = wardrobe_door_03_jan.FCStd
  Group = -> [LCS_Origin,Body,LCS_2]
  Origin = -> Origin001
  PartDescription = wardrobe_door_corpus02_jan
  PartID = wardrobe_door_03_jan
FEATURE [TechDraw::DrawSVGTemplate] Template  label="Vorlage"
  Height = 210
  Orientation = 1
  Template = <userpath>/scoop/apps/freecad/current/data/Mod/TechDraw/Templates/A4_Landscape_TD.svg
  Width = 297
FEATURE [TechDraw::DrawProjGroupItem] View
  CoarseView = false
  Direction = (-2e-16,0,-1)
  Focus = 100
  HardHidden = false
  IsoCount = 0
  IsoHidden = false
  IsoVisible = false
  LockPosition = false
  Perspective = false
  Rotation = 0
  RotationVector = (1,0,0)
  Scale = 0.1
  ScaleType = 2
  ScrubCount = 1
  SeamHidden = false
  SeamVisible = false
  SmoothHidden = false
  SmoothVisible = true
  Source = -> [wardrobe_door_03_jan]
  Type = 0
  X = 138.085
  XDirection = (2e-16,-1,0)
  Y = 151.508
FEATURE [TechDraw::DrawProjGroupItem] View001
  CoarseView = false
  Direction = (-1,1e-16,0)
  Focus = 100
  HardHidden = false
  IsoCount = 0
  IsoHidden = false
  IsoVisible = false
  LockPosition = false
  Perspective = false
  Rotation = 0
  RotationVector = (1,0,0)
  Scale = 0.1
  ScaleType = 2
  ScrubCount = 1
  SeamHidden = false
  SeamVisible = false
  SmoothHidden = false
  SmoothVisible = true
  Source = -> [wardrobe_door_03_jan]
  Type = 0
  X = 138.085
  XDirection = (-1e-16,-1,1e-16)
  Y = 98.1765
FEATURE [TechDraw::DrawViewAnnotation] Annotation  label="Beschriftung"
  Font = MS Shell Dlg 2
  LineSpace = 100
  LockPosition = false
  MaxWidth = -1
  Rotation = 0
  ScaleType = 0
  Text = Rev 01
  TextSize = 5
  TextStyle = 0
  X = 274.352
  Y = 62.5385
FEATURE [TechDraw::DrawViewDimension] Dimension  label="Maß"
  AngleOverride = false
  Arbitrary = false
  ArbitraryTolerances = false
  BoxCorners = (2) [(-39.0919,-25.75,0),(39.0919,25.75,0)]
  EqualTolerance = true
  ExtensionAngle = 0
  FormatSpec = %.1w
  FormatSpecOverTolerance = %+.1w
  FormatSpecUnderTolerance = %+.1w
  Inverted = false
  LineAngle = 0
  LockPosition = false
  MeasureType = 1
  OverTolerance = 0
  References2D = -> [View]
  Rotation = 0
  ScaleType = 0
  TheoreticalExact = false
  Type = 1
  UnderTolerance = 0
  X = 4.16935
  Y = -30.3138
FEATURE [TechDraw::DrawViewDimension] Dimension001  label="Maß001"
  AngleOverride = false
  Arbitrary = false
  ArbitraryTolerances = false
  BoxCorners = (2) [(-39.0919,-25.75,0),(39.0919,25.75,0)]
  EqualTolerance = true
  ExtensionAngle = 0
  FormatSpec = %.1w
  FormatSpecOverTolerance = %+.1w
  FormatSpecUnderTolerance = %+.1w
  Inverted = false
  LineAngle = 0
  LockPosition = false
  MeasureType = 1
  OverTolerance = 0
  References2D = -> [View]
  Rotation = 0
  ScaleType = 0
  TheoreticalExact = false
  Type = 2
  UnderTolerance = 0
  X = 52.2413
  Y = 0
FEATURE [TechDraw::DrawViewDimension] Dimension002  label="Maß002"
  AngleOverride = false
  Arbitrary = false
  ArbitraryTolerances = false
  BoxCorners = (2) [(-39.0919,-25.75,0),(39.0919,25.75,0)]
  EqualTolerance = true
  ExtensionAngle = 0
  FormatSpec = %.1w
  FormatSpecOverTolerance = %+.1w
  FormatSpecUnderTolerance = %+.1w
  Inverted = false
  LineAngle = 0
  LockPosition = false
  MeasureType = 1
  OverTolerance = 0
  References2D = -> [View]
  Rotation = 0
  ScaleType = 0
  TheoreticalExact = false
  Type = 1
  UnderTolerance = 0
  X = 30.1302
  Y = 42.2312
FEATURE [TechDraw::DrawViewDimension] Dimension003  label="Maß003"
  AngleOverride = false
  Arbitrary = false
  ArbitraryTolerances = false
  BoxCorners = (2) [(-39.0919,-25.75,0),(39.0919,25.75,0)]
  EqualTolerance = true
  ExtensionAngle = 0
  FormatSpec = (%.1w)
  FormatSpecOverTolerance = %+.1w
  FormatSpecUnderTolerance = %+.1w
  Inverted = false
  LineAngle = 0
  LockPosition = false
  MeasureType = 1
  OverTolerance = 0
  References2D = -> [View]
  Rotation = 0
  ScaleType = 0
  TheoreticalExact = false
  Type = 6
  UnderTolerance = 0
  X = 24.0227
  Y = 18.1693
FEATURE [TechDraw::DrawViewDimension] Dimension004  label="Maß004"
  AngleOverride = false
  Arbitrary = false
  ArbitraryTolerances = false
  BoxCorners = (2) [(-39.0919,-0.9,0),(39.0919,0.9,0)]
  EqualTolerance = true
  ExtensionAngle = 0
  FormatSpec = %.1w
  FormatSpecOverTolerance = %+.1w
  FormatSpecUnderTolerance = %+.1w
  Inverted = false
  LineAngle = 0
  LockPosition = false
  MeasureType = 1
  OverTolerance = 0
  References2D = -> [View001]
  Rotation = 0
  ScaleType = 0
  TheoreticalExact = false
  Type = 0
  UnderTolerance = 0
  X = 46.5954
  Y = -8.822
FEATURE [TechDraw::DrawViewDimension] Dimension005  label="Maß005"
  AngleOverride = false
  Arbitrary = false
  ArbitraryTolerances = false
  BoxCorners = (2) [(-39.0919,-25.75,0),(39.0919,25.75,0)]
  EqualTolerance = true
  ExtensionAngle = 0
  FormatSpec = (%.1w)
  FormatSpecOverTolerance = %+.1w
  FormatSpecUnderTolerance = %+.1w
  Inverted = false
  LineAngle = 0
  LockPosition = false
  MeasureType = 1
  OverTolerance = 0
  References2D = -> [View]
  Rotation = 0
  ScaleType = 0
  TheoreticalExact = false
  Type = 0
  UnderTolerance = 0
  X = -17.7962
  Y = 15.4858
FEATURE [TechDraw::DrawPage] Page  label="Seite"
  KeepUpdated = true
  NextBalloonIndex = 1
  ProjectionType = 0
  Template = -> Template
  Views = -> [View,View001,Annotation,Dimension,Dimension001,Dimension002,Dimension003,Dimension004,Dimension005]
---- part parts/wardrobe_left_corpus03_jan.FCStd = doc fcstd_53f12c202bbb ----
FCSTD DOCUMENT  (FreeCAD 1.0RUnknown)
Label: wardrobe_left_corpus03_jan
License: All rights reserved
objects: TechDraw::DrawViewDimension×4, PartDesign::CoordinateSystem×3, TechDraw::DrawProjGroupItem×2, Sketcher::SketchObject×1, PartDesign::Pad×1, PartDesign::Body×1, App::Part×1, TechDraw::DrawSVGTemplate×1, TechDraw::DrawPage×1
note: 15 computed .brp shape members not serialized (recipe doc carries the construction recipe); baked Part::Feature solids carry a one-line shape summary decoded from their .brp
EXTERNAL_REF file=../../mastersheet.FCStd obj=Spreadsheet
EXTERNAL_REF file=../../mastersketch.FCStd obj=Sketch
EXTERNAL_REF file=../../mastersketch.FCStd obj=Sketch001

FEATURE [Sketcher::SketchObject] Sketch
  ArcFitTolerance = 1e-06
  AttachmentSupport = -> [YZ_Plane]
  FullyConstrained = true
  MakeInternals = false
  MapMode = 5
  Placement = pos=(0,0,0) rot=(0.57735,0.57735,0.57735;2.0944rad)
  expr: Constraints[10] = mastersketch#<<corpus>>.Constraints.corpus03_left_height
  expr: Constraints[6] = mastersheet#Spreadsheet.corpus_outer_thickness
  expr: Constraints[9] = mastersketch#Sketch.Constraints.alpha
  sketch-geometry (4):
    g0: LineSegment StartX=0 StartY=0 StartZ=0 EndX=19 EndY=0 EndZ=0
    g1: LineSegment StartX=19 StartY=0 StartZ=0 EndX=19 EndY=150.296 EndZ=0
    g2: LineSegment StartX=0 StartY=128.064 StartZ=0 EndX=0 EndY=0 EndZ=0
    g3: LineSegment StartX=19 StartY=150.296 StartZ=0 EndX=0 EndY=128.064 EndZ=0
  constraints (12):
    c: Coincident(g0,g1)
    c: Coincident(g2,g0)
    c: Horizontal(g0)
    c: Vertical(g1)
    c: Vertical(g2)
    c: Coincident(g0,g-1)
    c: DistanceX(g0,g0) = 19
    c: Coincident(g3,g1)
    c: Coincident(g2,g3)
    c: Angle(g2,g3) = 2.43442
    c: DistanceY(g2,g2) = 128.064
    c: DistanceY(g1,g1) = 150.296  'max_height'
FEATURE [PartDesign::Pad] Pad
  Direction = (1,0,0)
  Length = 600
  Length2 = 10
  Placement = pos=(0,0,0) rot=(1,1,1;2.0944rad)
  Profile = -> Sketch
  ReferenceAxis = -> Sketch [N_Axis]
  Refine = true
  Suppressed = false
  Type = 0
  expr: Length = mastersheet#Spreadsheet.corpus_depth
FEATURE [PartDesign::Body] Body  label="wardrobe_left_corpus03_jan"
  AllowCompound = false
  Group = -> [Sketch,Pad]
  Origin = -> Origin
  Tip = -> Pad
FEATURE [PartDesign::CoordinateSystem] LCS_1  label="bottom"
  AttacherType = Attacher::AttachEngine3D
  AttachmentSupport = -> [Pad]
  MapMode = 45
  Placement = pos=(300,-6.66e-14,3.33e-14) rot=(0.57735,0.57735,0.57735;2.0944rad)
FEATURE [PartDesign::CoordinateSystem] LCS_2  label="top"
  AttacherType = Attacher::AttachEngine3D
  AttachmentOffset = pos=(0,0,0) rot=(0,0,1;0.863623rad)
  AttachmentSupport = -> [Pad]
  MapMode = 45
  Placement = pos=(300,-5.24e-14,128.064) rot=(0.684188,0.252533,0.684188;2.64687rad)
  expr: .AttachmentOffset.Rotation.Angle = mastersketch#Sketch.Constraints.alpha - 90 °
  expr: .AttachmentOffset.Rotation.Yaw = mastersketch#Sketch.Constraints.alpha - 90 °
FEATURE [PartDesign::CoordinateSystem] LCS_Origin
  AttacherType = Attacher::AttachEngine3D
  AttachmentSupport = -> [X_Axis001]
  MapMode = 2
FEATURE [App::Part] wardrobe_left_corpus03_jan  label="wardrobe_left_corpus03_jan001"
  DrawingName = wardrobe_left_corpus03_jan.FCStd
  Group = -> [LCS_Origin,LCS_1,LCS_2,Body]
  Origin = -> Origin001
  PartDescription = wardrobe_left_corpus03_jan
  PartID = wardrobe_left_corpus03_jan
FEATURE [TechDraw::DrawSVGTemplate] Template  label="Vorlage"
  Height = 210
  Orientation = 1
  Template = <userpath>/scoop/apps/freecad/current/data/Mod/TechDraw/Templates/A4_Landscape_TD.svg
  Width = 297
FEATURE [TechDraw::DrawProjGroupItem] View
  CoarseView = false
  Direction = (0,-1,0)
  Focus = 100
  HardHidden = false
  IsoCount = 0
  IsoHidden = false
  IsoVisible = false
  LockPosition = false
  Perspective = false
  Rotation = 0
  RotationVector = (1,0,0)
  Scale = 0.2
  ScaleType = 2
  ScrubCount = 1
  SeamHidden = false
  SeamVisible = false
  SmoothHidden = false
  SmoothVisible = true
  Source = -> [Body]
  Type = 0
  X = 99.704
  XDirection = (1,0,0)
  Y = 139.979
FEATURE [TechDraw::DrawProjGroupItem] View001
  CoarseView = false
  Direction = (-1,-1e-16,0)
  Focus = 100
  HardHidden = false
  IsoCount = 0
  IsoHidden = false
  IsoVisible = false
  LockPosition = false
  Perspective = false
  Rotation = 0
  RotationVector = (1,0,0)
  Scale = 0.2
  ScaleType = 2
  ScrubCount = 1
  SeamHidden = false
  SeamVisible = false
  SmoothHidden = false
  SmoothVisible = true
  Source = -> [Body]
  Type = 0
  X = 220.732
  XDirection = (1e-16,-1,0)
  Y = 139.979
FEATURE [TechDraw::DrawViewDimension] Dimension  label="Maß"
  AngleOverride = false
  Arbitrary = false
  ArbitraryTolerances = false
  BoxCorners = (2) [(-60,-15.0296,0),(60,15.0296,0)]
  EqualTolerance = true
  ExtensionAngle = 0
  FormatSpec = %.1w
  FormatSpecOverTolerance = %+.1w
  FormatSpecUnderTolerance = %+.1w
  Inverted = false
  LineAngle = 0
  LockPosition = false
  MeasureType = 1
  OverTolerance = 0
  References2D = -> [View]
  Rotation = 0
  ScaleType = 0
  TheoreticalExact = false
  Type = 1
  UnderTolerance = 0
  X = 0
  Y = -21.7911
FEATURE [TechDraw::DrawViewDimension] Dimension001  label="Maß001"
  AngleOverride = false
  Arbitrary = false
  ArbitraryTolerances = false
  BoxCorners = (2) [(-60,-15.0296,0),(60,15.0296,0)]
  EqualTolerance = true
  ExtensionAngle = 0
  FormatSpec = %.1w
  FormatSpecOverTolerance = %+.1w
  FormatSpecUnderTolerance = %+.1w
  Inverted = false
  LineAngle = 0
  LockPosition = false
  MeasureType = 1
  OverTolerance = 0
  References2D = -> [View]
  Rotation = 0
  ScaleType = 0
  TheoreticalExact = false
  Type = 0
  UnderTolerance = 0
  X = 72.8143
  Y = 0
FEATURE [TechDraw::DrawViewDimension] Dimension002  label="Maß002"
  AngleOverride = false
  Arbitrary = false
  ArbitraryTolerances = false
  BoxCorners = (2) [(-1.9,-15.0296,0),(1.9,15.0296,0)]
  EqualTolerance = true
  ExtensionAngle = 0
  FormatSpec = %.1w
  FormatSpecOverTolerance = %+.1w
  FormatSpecUnderTolerance = %+.1w
  Inverted = false
  LineAngle = 0
  LockPosition = false
  MeasureType = 1
  OverTolerance = 0
  References2D = -> [View001]
  Rotation = 0
  ScaleType = 0
  TheoreticalExact = false
  Type = 0
  UnderTolerance = 0
  X = 20.5059
  Y = -26.6941
FEATURE [TechDraw::DrawViewDimension] Dimension003  label="Maß003"
  AngleOverride = false
  Arbitrary = false
  ArbitraryTolerances = false
  BoxCorners = (2) [(-1.9,-15.0296,0),(1.9,15.0296,0)]
  EqualTolerance = true
  ExtensionAngle = 0
  FormatSpec = %.1w
  FormatSpecOverTolerance = %+.1w
  FormatSpecUnderTolerance = %+.1w
  Inverted = false
  LineAngle = 0
  LockPosition = false
  MeasureType = 1
  OverTolerance = 0
  References2D = -> [View001]
  Rotation = 0
  ScaleType = 0
  TheoreticalExact = false
  Type = 6
  UnderTolerance = 0
  X = 28.0714
  Y = 5.82284
FEATURE [TechDraw::DrawPage] Page  label="Seite"
  KeepUpdated = true
  NextBalloonIndex = 1
  ProjectionType = 0
  Template = -> Template
  Views = -> [View,View001,Dimension,Dimension001,Dimension002,Dimension003]
---- part parts/wardrobe_right_corpus03_jan.FCStd = doc fcstd_ac50fb12b202 ----
FCSTD DOCUMENT  (FreeCAD 1.0RUnknown)
Label: wardrobe_right_corpus03_jan
License: All rights reserved
LicenseURL: https://en.wikipedia.org/wiki/All_rights_reserved
objects: TechDraw::DrawViewDimension×4, PartDesign::CoordinateSystem×2, TechDraw::DrawProjGroupItem×2, Sketcher::SketchObject×1, PartDesign::Pad×1, PartDesign::Body×1, App::Part×1, TechDraw::DrawSVGTemplate×1, TechDraw::DrawPage×1
note: 14 computed .brp shape members not serialized (recipe doc carries the construction recipe); baked Part::Feature solids carry a one-line shape summary decoded from their .brp
EXTERNAL_REF file=../../mastersheet.FCStd obj=Spreadsheet
EXTERNAL_REF file=../../mastersketch.FCStd obj=Sketch
EXTERNAL_REF file=../../mastersketch.FCStd obj=Sketch001

FEATURE [Sketcher::SketchObject] Sketch
  ArcFitTolerance = 1e-06
  AttachmentSupport = -> [XZ_Plane004]
  FullyConstrained = true
  MakeInternals = false
  MapMode = 5
  Placement = pos=(0,0,0) rot=(1,0,0;1.5708rad)
  expr: Constraints[10] = mastersketch#<<corpus>>.Constraints.corpus03_right_height
  expr: Constraints[6] = mastersheet#Spreadsheet.corpus_outer_thickness
  expr: Constraints[9] = mastersketch#Sketch.Constraints.alpha
  sketch-geometry (4):
    g0: LineSegment StartX=0 StartY=0 StartZ=0 EndX=0 EndY=736.518 EndZ=0
    g1: LineSegment StartX=-19 StartY=714.286 StartZ=0 EndX=-19 EndY=0 EndZ=0
    g2: LineSegment StartX=-19 StartY=0 StartZ=0 EndX=0 EndY=0 EndZ=0
    g3: LineSegment StartX=0 StartY=736.518 StartZ=0 EndX=-19 EndY=714.286 EndZ=0
  constraints (11):
    c: Coincident(g1,g2)
    c: Coincident(g2,g0)
    c: Vertical(g0)
    c: Vertical(g1)
    c: Horizontal(g2)
    c: Coincident(g0,g-1)
    c: DistanceX(g2,g2) = 19
    c: Coincident(g3,g0)
    c: Coincident(g1,g3)
    c: Angle(g1,g3) = 2.43442
    c: DistanceY(g0,g0) = 736.518
FEATURE [PartDesign::Pad] Pad
  Direction = (0,-1,2e-16)
  Length = 600
  Length2 = 10
  Placement = pos=(0,0,0) rot=(1,0,0;1.5708rad)
  Profile = -> Sketch
  ReferenceAxis = -> Sketch [N_Axis]
  Refine = true
  Suppressed = false
  Type = 0
  expr: Length = mastersheet#Spreadsheet.corpus_depth
FEATURE [PartDesign::Body] Body002  label="wardrobe_right_corpus03_jan"
  AllowCompound = false
  Group = -> [Sketch,Pad]
  Origin = -> Origin004
  Tip = -> Pad
FEATURE [PartDesign::CoordinateSystem] LCS_1
  AttacherType = Attacher::AttachEngine3D
  AttachmentSupport = -> [Pad]
  MapMode = 45
  Placement = pos=(0,-300,6.66e-14) rot=(0,0.707107,0.707107;3.14159rad)
FEATURE [PartDesign::CoordinateSystem] LCS_Origin
  AttacherType = Attacher::AttachEngine3D
  AttachmentSupport = -> [X_Axis]
  MapMode = 2
FEATURE [App::Part] wardrobe_right_corpus03_jan  label="wardrobe_right_corpus03_jan001"
  DrawingName = wardrobe_right_corpus03_jan.FCStd
  Group = -> [LCS_Origin,Body002,LCS_1]
  Origin = -> Origin
  PartDescription = wardrobe_right_corpus03_jan
  PartID = wardrobe_right_corpus03_jan
FEATURE [TechDraw::DrawSVGTemplate] Template  label="Vorlage"
  Height = 210
  Orientation = 1
  Template = <userpath>/scoop/apps/freecad/current/data/Mod/TechDraw/Templates/A4_Landscape_TD.svg
  Width = 297
FEATURE [TechDraw::DrawProjGroupItem] View
  CoarseView = false
  Direction = (-2e-16,1,0)
  Focus = 100
  HardHidden = false
  IsoCount = 0
  IsoHidden = false
  IsoVisible = false
  LockPosition = false
  Perspective = false
  Rotation = 0
  RotationVector = (1,0,0)
  Scale = 0.1
  ScaleType = 2
  ScrubCount = 1
  SeamHidden = false
  SeamVisible = false
  SmoothHidden = false
  SmoothVisible = true
  Source = -> [Body002]
  Type = 0
  X = 207.757
  XDirection = (-1,-2e-16,0)
  Y = 132.115
FEATURE [TechDraw::DrawProjGroupItem] View001
  CoarseView = false
  Direction = (-1,-1e-16,0)
  Focus = 100
  HardHidden = false
  IsoCount = 0
  IsoHidden = false
  IsoVisible = false
  LockPosition = false
  Perspective = false
  Rotation = 0
  RotationVector = (1,0,0)
  Scale = 0.1
  ScaleType = 2
  ScrubCount = 1
  SeamHidden = false
  SeamVisible = false
  SmoothHidden = false
  SmoothVisible = true
  Source = -> [Body002]
  Type = 0
  X = 107.559
  XDirection = (1e-16,-1,0)
  Y = 132.115
FEATURE [TechDraw::DrawViewDimension] Dimension  label="Maß"
  AngleOverride = false
  Arbitrary = false
  ArbitraryTolerances = false
  BoxCorners = (2) [(-30,-36.8259,0),(30,36.8259,0)]
  EqualTolerance = true
  ExtensionAngle = 0
  FormatSpec = %.1w
  FormatSpecOverTolerance = %+.1w
  FormatSpecUnderTolerance = %+.1w
  Inverted = false
  LineAngle = 0
  LockPosition = false
  MeasureType = 1
  OverTolerance = 0
  References2D = -> [View001]
  Rotation = 0
  ScaleType = 0
  TheoreticalExact = false
  Type = 1
  UnderTolerance = 0
  X = 0
  Y = -42.401
FEATURE [TechDraw::DrawViewDimension] Dimension001  label="Maß001"
  AngleOverride = false
  Arbitrary = false
  ArbitraryTolerances = false
  BoxCorners = (2) [(-30,-36.8259,0),(30,36.8259,0)]
  EqualTolerance = true
  ExtensionAngle = 0
  FormatSpec = %.1w
  FormatSpecOverTolerance = %+.1w
  FormatSpecUnderTolerance = %+.1w
  Inverted = false
  LineAngle = 0
  LockPosition = false
  MeasureType = 1
  OverTolerance = 0
  References2D = -> [View001]
  Rotation = 0
  ScaleType = 0
  TheoreticalExact = false
  Type = 0
  UnderTolerance = 0
  X = 43.6616
  Y = 0
FEATURE [TechDraw::DrawViewDimension] Dimension002  label="Maß002"
  AngleOverride = false
  Arbitrary = false
  ArbitraryTolerances = false
  BoxCorners = (2) [(-0.95,-36.8259,0),(0.95,36.8259,0)]
  EqualTolerance = true
  ExtensionAngle = 0
  FormatSpec = %.1w
  FormatSpecOverTolerance = %+.1w
  FormatSpecUnderTolerance = %+.1w
  Inverted = false
  LineAngle = 0
  LockPosition = false
  MeasureType = 1
  OverTolerance = 0
  References2D = -> [View]
  Rotation = 0
  ScaleType = 0
  TheoreticalExact = false
  Type = 0
  UnderTolerance = 0
  X = 12.357
  Y = -45.6451
FEATURE [TechDraw::DrawViewDimension] Dimension003  label="Maß003"
  AngleOverride = false
  Arbitrary = false
  ArbitraryTolerances = false
  BoxCorners = (2) [(-0.95,-36.8259,0),(0.95,36.8259,0)]
  EqualTolerance = true
  ExtensionAngle = 0
  FormatSpec = %.1w
  FormatSpecOverTolerance = %+.1w
  FormatSpecUnderTolerance = %+.1w
  Inverted = false
  LineAngle = 0
  LockPosition = false
  MeasureType = 1
  OverTolerance = 0
  References2D = -> [View]
  Rotation = 0
  ScaleType = 0
  TheoreticalExact = false
  Type = 6
  UnderTolerance = 0
  X = 14.3684
  Y = 3.37588
FEATURE [TechDraw::DrawPage] Page  label="Seite"
  KeepUpdated = true
  NextBalloonIndex = 1
  ProjectionType = 0
  Template = -> Template
  Views = -> [View,View001,Dimension,Dimension001,Dimension002,Dimension003]
---- part parts/wardrobe_top_corpus03_jan.FCStd = doc fcstd_2eebeba2e3b1 ----
FCSTD DOCUMENT  (FreeCAD 1.0RUnknown)
Label: wardrobe_top_corpus03_jan
License: All rights reserved
objects: TechDraw::DrawViewDimension×5, PartDesign::CoordinateSystem×3, TechDraw::DrawProjGroupItem×2, Sketcher::SketchObject×1, PartDesign::Pad×1, PartDesign::Body×1, App::Part×1, TechDraw::DrawSVGTemplate×1, TechDraw::DrawPage×1
note: 18 computed .brp shape members not serialized (recipe doc carries the construction recipe); baked Part::Feature solids carry a one-line shape summary decoded from their .brp
EXTERNAL_REF file=../../mastersheet.FCStd obj=Spreadsheet
EXTERNAL_REF file=../../mastersketch.FCStd obj=Sketch

FEATURE [Sketcher::SketchObject] Sketch
  ArcFitTolerance = 1e-06
  AttachmentSupport = -> [XZ_Plane]
  FullyConstrained = true
  MakeInternals = false
  MapMode = 5
  Placement = pos=(0,0,0) rot=(1,0,0;1.5708rad)
  expr: Constraints[14] = mastersketch#Sketch.Constraints.alpha
  expr: Constraints[22] = (mastersketch#Sketch.Constraints.corpus03_door_width + 5 mm) / cos(mastersketch#Sketch.Constraints.alpha - 90 °)
  expr: Constraints[3] = mastersheet#Spreadsheet.corpus_outer_thickness
  sketch-geometry (9):
    g0: LineSegment StartX=-411.308 StartY=-9.5 StartZ=0 EndX=389.076 EndY=-9.5 EndZ=0
    g1: LineSegment StartX=411.308 StartY=9.5 StartZ=0 EndX=-389.076 EndY=9.5 EndZ=0
    g2: GeomPoint [constr] X=0 Y=0 Z=0
    g3: LineSegment StartX=-411.308 StartY=-9.5 StartZ=0 EndX=-389.076 EndY=9.5 EndZ=0
    g4: LineSegment StartX=411.308 StartY=9.5 StartZ=0 EndX=389.076 EndY=-9.5 EndZ=0
    g5: LineSegment [constr] StartX=0 StartY=0 StartZ=0 EndX=0 EndY=9.5 EndZ=0
    g6: LineSegment [constr] StartX=0 StartY=0 StartZ=0 EndX=0 EndY=-9.5 EndZ=0
    g7: LineSegment [constr] StartX=0 StartY=0 StartZ=0 EndX=-400.192 EndY=-3e-16 EndZ=0
    g8: LineSegment [constr] StartX=0 StartY=0 StartZ=0 EndX=400.192 EndY=7.9e-15 EndZ=0
  constraints (24):
    c: Horizontal(g0)
    c: Horizontal(g1)
    c: Coincident(g2,g-1)
    c: Distance(g0,g1) = 19
    c: Coincident(g1,g3)
    c: Coincident(g0,g4)
    c: Parallel(g3,g4)
    c: Coincident(g4,g1)
    c: Coincident(g5,g2)
    c: PointOnObject(g5,g1)
    c: Vertical(g5)
    c: Vertical(g6)
    c: Equal(g5,g6)
    c: Coincident(g0,g3)
    c: Angle(g3,g1) = 2.43442
    c: PointOnObject(g6,g0)
    c: Coincident(g6,g2)
    c: Coincident(g7,g2)
    c: Symmetric(g3,g3,g7)
    c: Coincident(g8,g2)
    c: Symmetric(g4,g4,g8)
    c: Equal(g7,g8)
    c: DistanceX(g0,g0) = 800.385
    c: DistanceX(g0,g1) = 822.617  'max_length'
FEATURE [PartDesign::Pad] Pad
  Direction = (0,-1,2e-16)
  Length = 600
  Length2 = 10
  Placement = pos=(0,0,0) rot=(1,0,0;1.5708rad)
  Profile = -> Sketch
  ReferenceAxis = -> Sketch [N_Axis]
  Refine = true
  Suppressed = false
  Type = 0
  expr: Length = mastersheet#Spreadsheet.corpus_depth
FEATURE [PartDesign::Body] Body  label="wardrobe_top_corpus03_jan"
  AllowCompound = false
  Group = -> [Sketch,Pad]
  Origin = -> Origin
  Tip = -> Pad
FEATURE [PartDesign::CoordinateSystem] LCS_1
  AttacherType = Attacher::AttachEngine3D
  AttachmentSupport = -> [Pad]
  MapMode = 45
  Placement = pos=(-411.308,-300,-9.5) rot=(0,0.707107,0.707107;3.14159rad)
FEATURE [PartDesign::CoordinateSystem] LCS_Origin
  AttacherType = Attacher::AttachEngine3D
  AttachmentSupport = -> [X_Axis001]
  MapMode = 2
FEATURE [PartDesign::CoordinateSystem] LCS_2
  AttacherType = Attacher::AttachEngine3D
  AttachmentSupport = -> [Pad]
  MapMode = 7
  Placement = pos=(-389.076,-600,9.5) rot=(0.57735,0.57735,0.57735;2.0944rad)
FEATURE [App::Part] wardrobe_top_corpus03_jan  label="wardrobe_top_corpus03_jan001"
  DrawingName = wardrobe_top_corpus03_jan.FCStd
  Group = -> [LCS_Origin,LCS_2,LCS_1,Body]
  Origin = -> Origin001
  PartDescription = wardrobe_top_corpus03_jan
  PartID = wardrobe_top_corpus03_jan
FEATURE [TechDraw::DrawSVGTemplate] Template  label="Vorlage"
  Height = 210
  Orientation = 1
  Template = <userpath>/scoop/apps/freecad/current/data/Mod/TechDraw/Templates/A4_Landscape_TD.svg
  Width = 297
FEATURE [TechDraw::DrawProjGroupItem] View
  CoarseView = false
  Direction = (0,-1,0)
  Focus = 100
  HardHidden = false
  IsoCount = 0
  IsoHidden = false
  IsoVisible = false
  LockPosition = false
  Perspective = false
  Rotation = 0
  RotationVector = (1,0,0)
  Scale = 0.1
  ScaleType = 2
  ScrubCount = 1
  SeamHidden = false
  SeamVisible = false
  SmoothHidden = false
  SmoothVisible = true
  Source = -> [wardrobe_top_corpus03_jan]
  Type = 0
  X = 179.23
  XDirection = (1e-16,0,-1)
  Y = 137.322
FEATURE [TechDraw::DrawProjGroupItem] View001
  CoarseView = false
  Direction = (0,0,-1)
  Focus = 100
  HardHidden = false
  IsoCount = 0
  IsoHidden = false
  IsoVisible = false
  LockPosition = false
  Perspective = false
  Rotation = 0
  RotationVector = (1,0,0)
  Scale = 0.1
  ScaleType = 2
  ScrubCount = 1
  SeamHidden = false
  SeamVisible = false
  SmoothHidden = false
  SmoothVisible = true
  Source = -> [wardrobe_top_corpus03_jan]
  Type = 0
  X = 80.4098
  XDirection = (-3e-16,1,0)
  Y = 137.322
FEATURE [TechDraw::DrawViewDimension] Dimension  label="Maß"
  AngleOverride = false
  Arbitrary = false
  ArbitraryTolerances = false
  BoxCorners = (2) [(-30,-41.1308,0),(30,41.1308,0)]
  EqualTolerance = true
  ExtensionAngle = 0
  FormatSpec = %.1w
  FormatSpecOverTolerance = %+.1w
  FormatSpecUnderTolerance = %+.1w
  Inverted = false
  LineAngle = 0
  LockPosition = false
  MeasureType = 1
  OverTolerance = 0
  References2D = -> [View001]
  Rotation = 0
  ScaleType = 0
  TheoreticalExact = false
  Type = 1
  UnderTolerance = 0
  X = 0
  Y = -46.7106
FEATURE [TechDraw::DrawViewDimension] Dimension001  label="Maß001"
  AngleOverride = false
  Arbitrary = false
  ArbitraryTolerances = false
  BoxCorners = (2) [(-30,-41.1308,0),(30,41.1308,0)]
  EqualTolerance = true
  ExtensionAngle = 0
  FormatSpec = %.1w
  FormatSpecOverTolerance = %+.1w
  FormatSpecUnderTolerance = %+.1w
  Inverted = false
  LineAngle = 0
  LockPosition = false
  MeasureType = 1
  OverTolerance = 0
  References2D = -> [View001]
  Rotation = 0
  ScaleType = 0
  TheoreticalExact = false
  Type = 0
  UnderTolerance = 0
  X = 51.2409
  Y = -10.3819
FEATURE [TechDraw::DrawViewDimension] Dimension003  label="Maß003"
  AngleOverride = false
  Arbitrary = false
  ArbitraryTolerances = false
  BoxCorners = (2) [(-0.95,-41.1308,0),(0.95,41.1308,0)]
  EqualTolerance = true
  ExtensionAngle = 0
  FormatSpec = %.1w
  FormatSpecOverTolerance = %+.1w
  FormatSpecUnderTolerance = %+.1w
  Inverted = false
  LineAngle = 0
  LockPosition = false
  MeasureType = 1
  OverTolerance = 0
  References2D = -> [View]
  Rotation = 0
  ScaleType = 0
  TheoreticalExact = false
  Type = 6
  UnderTolerance = 0
  X = 16.0781
  Y = 5.68594
FEATURE [TechDraw::DrawViewDimension] Dimension004  label="Maß004"
  AngleOverride = false
  Arbitrary = false
  ArbitraryTolerances = false
  BoxCorners = (2) [(-0.95,-41.1308,0),(0.95,41.1308,0)]
  EqualTolerance = true
  ExtensionAngle = 0
  FormatSpec = %.1w
  FormatSpecOverTolerance = %+.1w
  FormatSpecUnderTolerance = %+.1w
  Inverted = false
  LineAngle = 0
  LockPosition = false
  MeasureType = 1
  OverTolerance = 0
  References2D = -> [View]
  Rotation = 0
  ScaleType = 0
  TheoreticalExact = false
  Type = 0
  UnderTolerance = 0
  X = 9.01033
  Y = 59.2546
FEATURE [TechDraw::DrawViewDimension] Dimension006  label="Maß006"
  AngleOverride = false
  Arbitrary = false
  ArbitraryTolerances = false
  BoxCorners = (2) [(-0.95,-41.1308,0),(0.95,41.1308,0)]
  EqualTolerance = true
  ExtensionAngle = 0
  FormatSpec = %.1w
  FormatSpecOverTolerance = %+.1w
  FormatSpecUnderTolerance = %+.1w
  Inverted = false
  LineAngle = 0
  LockPosition = false
  MeasureType = 1
  OverTolerance = 0
  References2D = -> [View]
  Rotation = 0
  ScaleType = 0
  TheoreticalExact = false
  Type = 6
  UnderTolerance = 0
  X = -16.1416
  Y = 14.6144
FEATURE [TechDraw::DrawPage] Page  label="Seite"
  KeepUpdated = true
  NextBalloonIndex = 1
  ProjectionType = 0
  Template = -> Template
  Views = -> [View,View001,Dimension,Dimension001,Dimension003,Dimension004,Dimension006]
